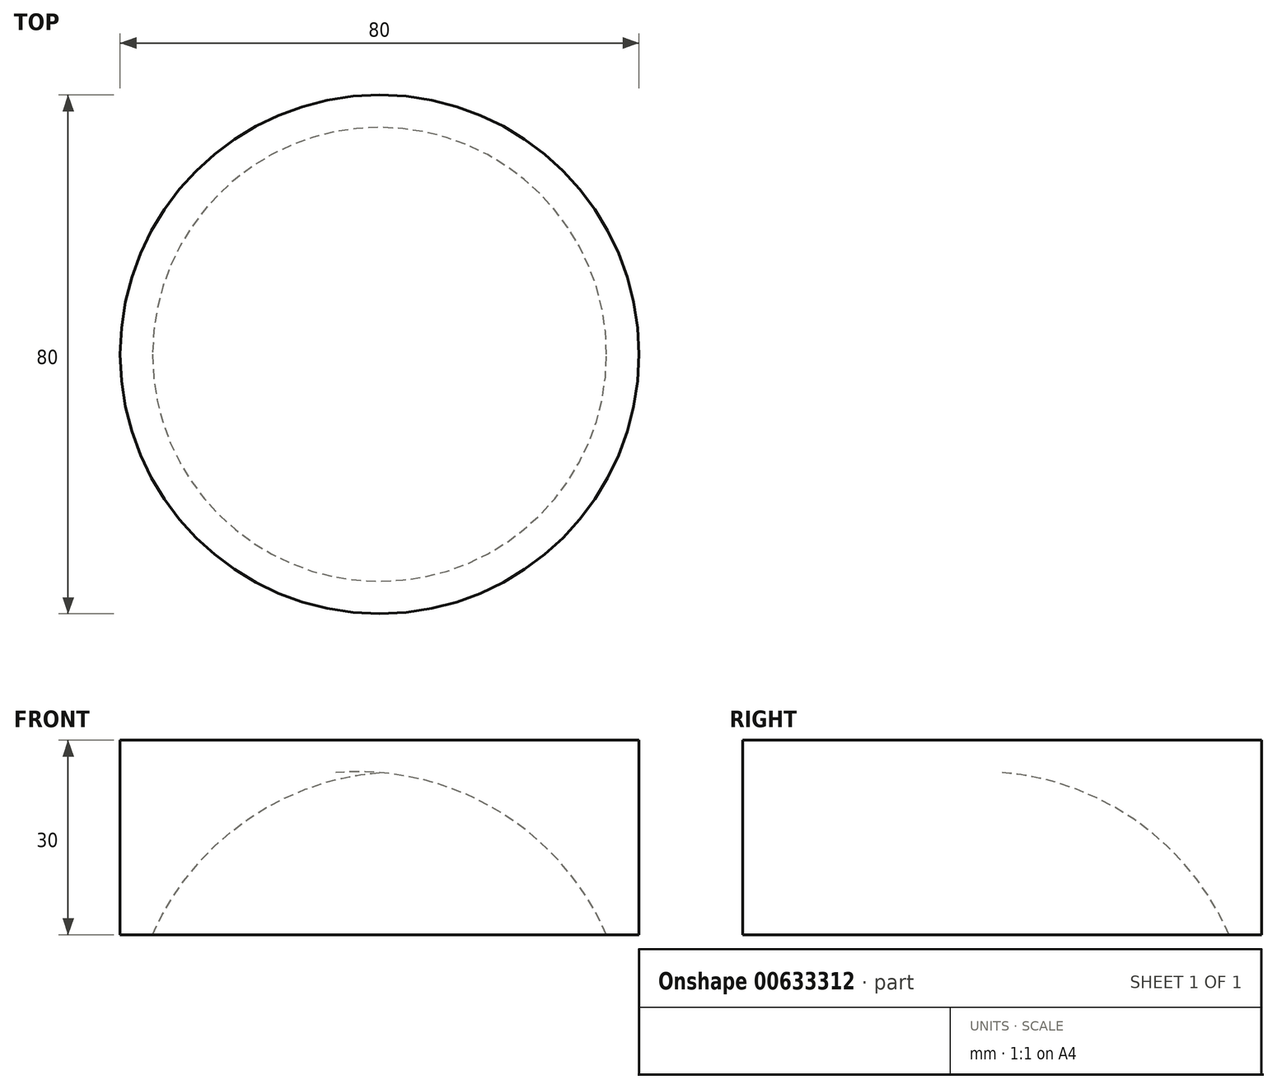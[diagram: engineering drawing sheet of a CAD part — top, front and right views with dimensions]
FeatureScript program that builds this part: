
annotation { "Feature Type Name" : "Feature", "Feature Type Description" : "" }
export const myFeature = defineFeature(function(context is Context, id is Id, definition is map)
    precondition{}
    {
        {
            var Q0;
            Q0=qCreatedBy(makeId("Front.planeOp"),FACE);
            var sketch = newSketch(context, id + "F0", { "sketchPlane" : qUnion([Q0])});
            skPoint(sketch, "E0.start.orphan", {"position": v(0, 0) * mm});
            skArc(sketch, "E1", {"start": v(0, 25) * mm, "mid": v(-20.96, 17.34) * mm, "end": v(-35, 0) * mm});
            skLineSegment(sketch, "E2", {"start": v(0, 25) * mm, "end": v(0, 30) * mm});
            skLineSegment(sketch, "E3", {"start": v(-35, 0) * mm, "end": v(-40, 0) * mm});
            skLineSegment(sketch, "E4", {"start": v(-40, 0) * mm, "end": v(-40, 30) * mm});
            skLineSegment(sketch, "E5", {"start": v(0, 30) * mm, "end": v(-40, 30) * mm});
            skSolve(sketch);
        }
        {
            var Q0;
            Q0=makeQuery(id+"F0.imprint","IMPRINT",FACE,{"disambiguationData":[TD([[makeQuery(id+"F0.imprint","IMPRINT",EDGE,{"derivedFrom":sQuery(id+"F0.wireOp",EDGE,"E1")}),-1.0]])]});
            var Q1;
            Q1=sQuery(id+"F0.wireOp",EDGE,"E2");
            revolve(context, id + "F1", {"entities" : qUnion([Q0]), "axis" : qUnion([Q1]), "revolveType" : RevolveType.FULL});
        }
    });
